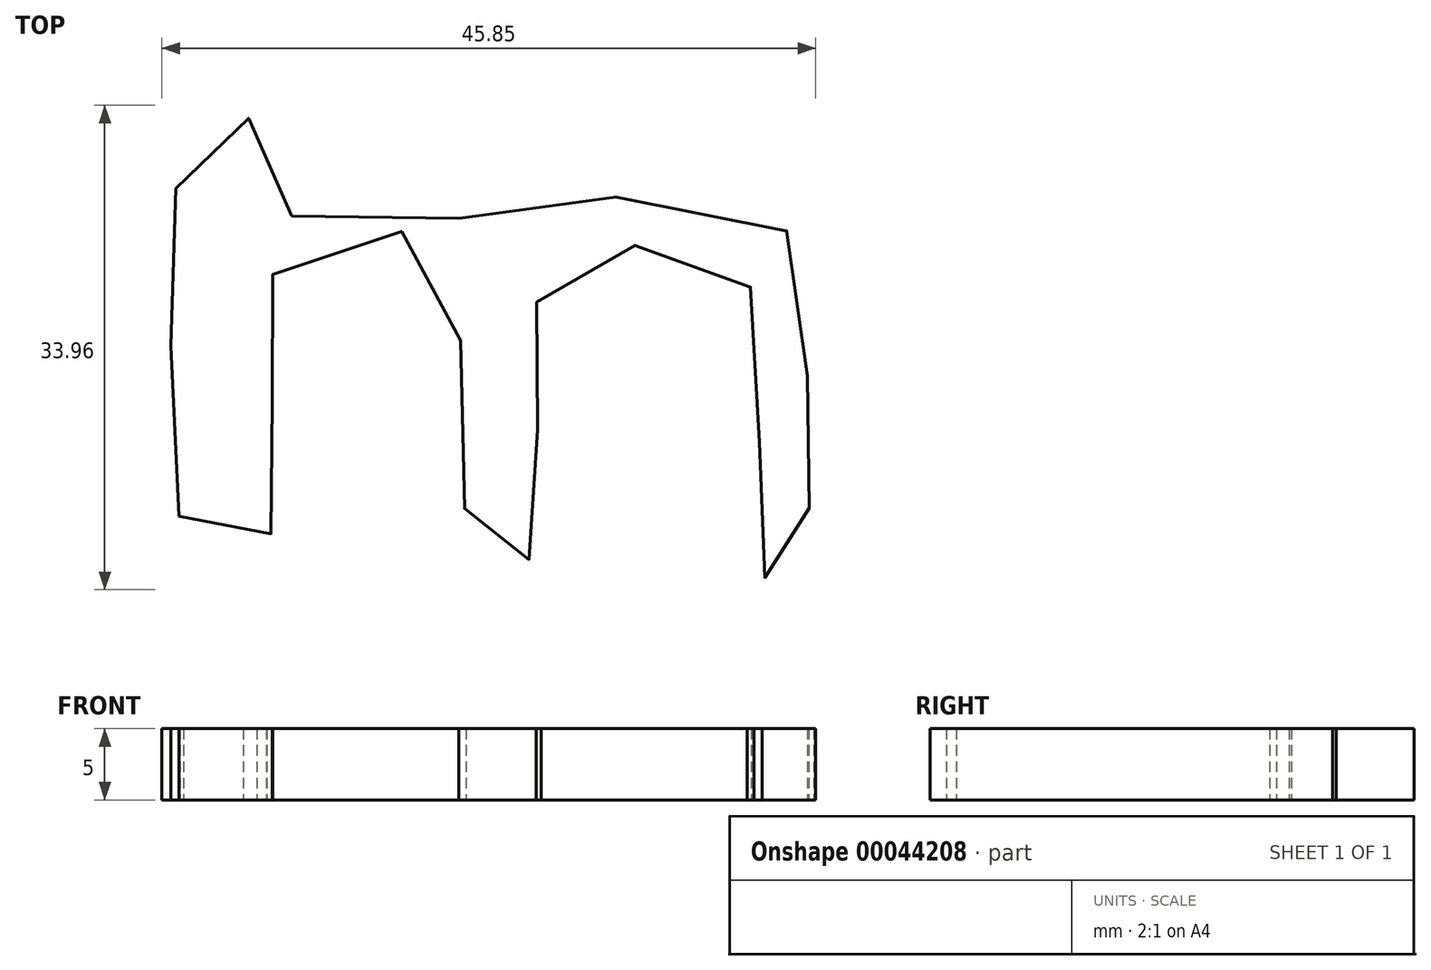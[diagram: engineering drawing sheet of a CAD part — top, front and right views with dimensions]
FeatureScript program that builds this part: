
annotation { "Feature Type Name" : "Feature", "Feature Type Description" : "" }
export const myFeature = defineFeature(function(context is Context, id is Id, definition is map)
    precondition{}
    {
        {
            var Q0;
            Q0=qCreatedBy(makeId("Top.planeOp"),FACE);
            var sketch = newSketch(context, id + "F0", { "sketchPlane" : qUnion([Q0])});
            skFitSpline(sketch, "E0", {"points": [v(-57.28, 32.14) * mm, v(-57.28, 26.5) * mm, v(-57.55, 19.77) * mm, v(-56.75, 13.04) * mm, v(-56.2, 6.59) * mm, v(-50.83, 6.59) * mm, v(-50.83, 9) * mm, v(-50.56, 13.58) * mm, v(-50.56, 17.88) * mm, v(-50.83, 22.19) * mm, v(-50.56, 25.95) * mm, v(-47.33, 28.64) * mm, v(-41.69, 29.18) * mm, v(-38.46, 27.03) * mm, v(-37.38, 22.46) * mm, v(-37.11, 16.54) * mm, v(-37.11, 9) * mm, v(-37.11, 6.05) * mm, v(-33.08, 5.51) * mm, v(-32, 9.55) * mm, v(-32, 13.58) * mm, v(-31.74, 17.35) * mm, v(-31.74, 21.38) * mm, v(-31.74, 25.15) * mm, v(-29.05, 27.03) * mm, v(-25.28, 28.1) * mm, v(-20.98, 28.1) * mm, v(-17.21, 25.95) * mm, v(-17.21, 21.11) * mm, v(-16.4, 14.66) * mm, v(-16.4, 8.2) * mm, v(-16.4, 5.24) * mm, v(-12.9, 4.17) * mm, v(-12.64, 7.66) * mm, v(-12.9, 11.7) * mm, v(-12.9, 16) * mm, v(-12.9, 21.11) * mm, v(-12.9, 27.3) * mm, v(-17.48, 30.8) * mm, v(-25.55, 31.87) * mm, v(-34.42, 27.84) * mm, v(-38.73, 31.33) * mm, v(-45.45, 31.87) * mm, v(-52.44, 29.45) * mm, v(-51.9, 36.71) * mm, v(-57.82, 36.98) * mm, v(-57.28, 32.14) * mm]});
            skSolve(sketch);
        }
        {
            var Q0;
            Q0=makeQuery(id+"F0.imprint","IMPRINT",FACE,{"disambiguationData":[TD([[makeQuery(id+"F0.imprint","IMPRINT",EDGE,{"derivedFrom":sQuery(id+"F0.wireOp",EDGE,"E0")}),1.0]])]});
            extrude(context, id + "F1", {"entities" : qUnion([Q0]), "depth" : 5 * mm});
        }
    });
